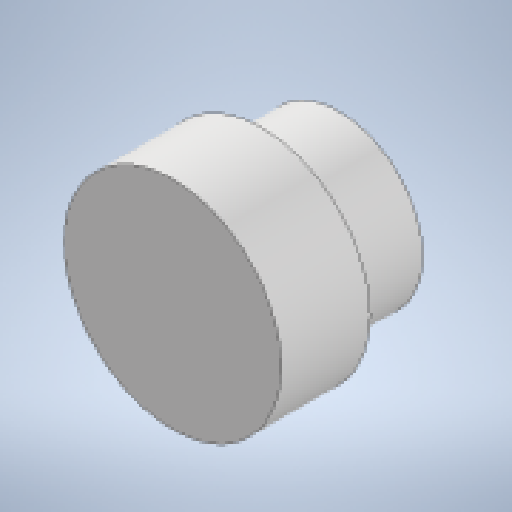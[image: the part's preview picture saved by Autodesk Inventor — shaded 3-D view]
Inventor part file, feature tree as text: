
AUTODESK INVENTOR PART (.ipt)
format: ipt  version: 2023 (Build 270158000, 158)  size: 147,968 bytes
history: native  units: in
note: dims shown in document units (in); Inventor stores cm internally (conversion verified against a paired STEP export)
features: extrude x3, sketch x2, plane x1
ambient origin geometry x8: Origin, YZ Plane, XZ Plane, XY Plane, X Axis, Y Axis, Z Axis, Center Point
bodies: Solid1 (feature_tree)
feature tree (6):
  plane  "Work Plane1"
  sketch  "Sketch1"  dims[d0=0.7677in d1=0.5906in]
  extrude  "Extrusion1"  Depth=0.5906in
  extrude  "Extrusion2"  Depth=0.5906in TaperAngle=0.0deg
  extrude  "Extrusion3"  Depth=0.5906in
  sketch  "Sketch2"  dims[d2=1.0in d3=0.0in d4=0.5906in d5=0.0in d6=0.1378in d7=0.1575in d8=0.315in d9=0.0in d10=0.0in]
